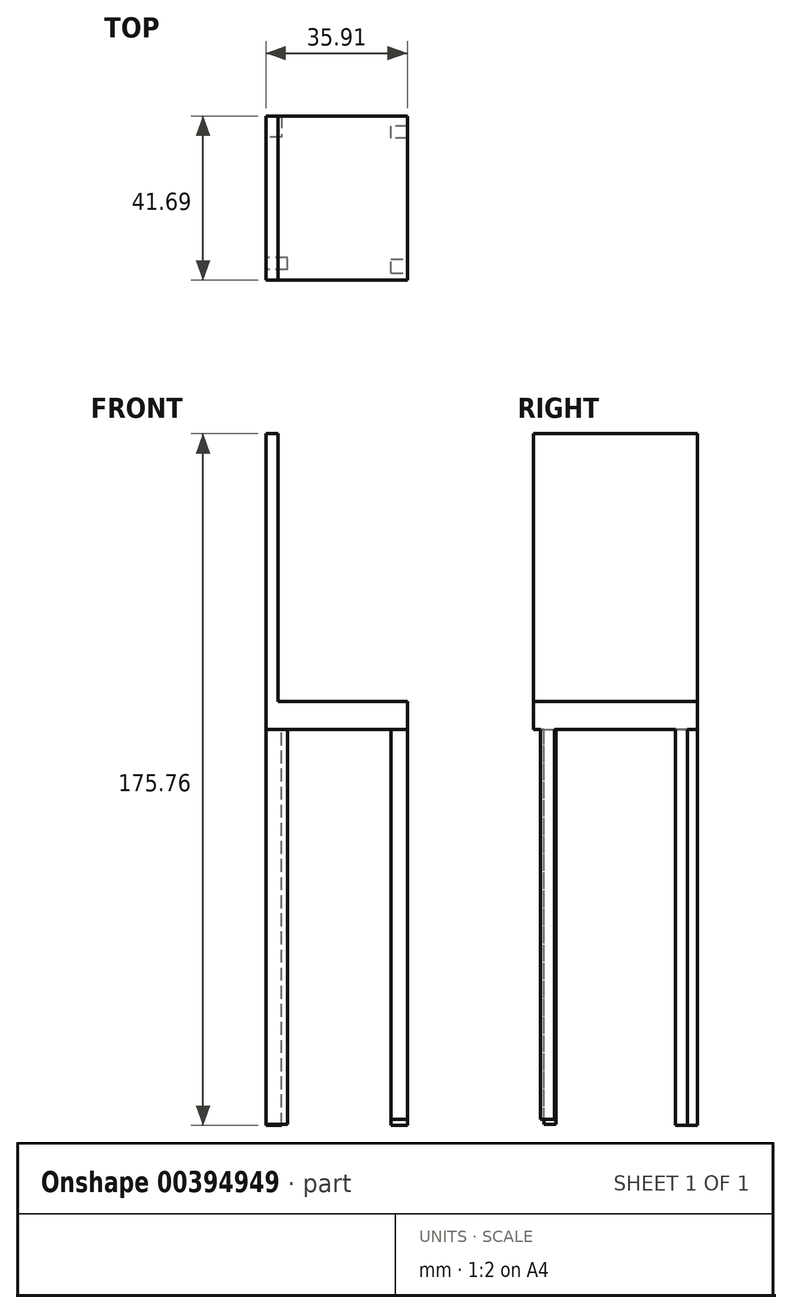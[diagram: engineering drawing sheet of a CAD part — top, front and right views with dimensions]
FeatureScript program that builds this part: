
annotation { "Feature Type Name" : "Feature", "Feature Type Description" : "" }
export const myFeature = defineFeature(function(context is Context, id is Id, definition is map)
    precondition{}
    {
        {
            var Q0;
            Q0=qCreatedBy(makeId("Top.planeOp"),FACE);
            var sketch = newSketch(context, id + "F0", { "sketchPlane" : qUnion([Q0])});
            skLineSegment(sketch, "E0.bottom", {"start": v(-61.68, 12.98) * mm, "end": v(-25.77, 12.98) * mm});
            skLineSegment(sketch, "E0.top", {"start": v(-61.68, -28.7) * mm, "end": v(-25.77, -28.7) * mm});
            skLineSegment(sketch, "E0.left", {"start": v(-61.68, 12.98) * mm, "end": v(-61.68, -28.7) * mm});
            skLineSegment(sketch, "E0.right", {"start": v(-25.77, 12.98) * mm, "end": v(-25.77, -28.7) * mm});
            skSolve(sketch);
        }
        {
            var Q0;
            Q0 = qSketchRegion(id + "F0", true);
            extrude(context, id + "F1", {"entities" : qUnion([Q0]), "depth" : 7.11 * mm});
        }
        {
            var Q0;
            Q0=makeQuery(id+"F1.opExtrude","CAP_FACE",FACE,{"disambiguationData":[OSD([sQuery(id+"F0.wireOp",EDGE,"E0.bottom"),sQuery(id+"F0.wireOp",EDGE,"E0.top"),sQuery(id+"F0.wireOp",EDGE,"E0.left"),sQuery(id+"F0.wireOp",EDGE,"E0.right")])],"isStart":true});
            var sketch = newSketch(context, id + "F2", { "sketchPlane" : qUnion([Q0])});
            skLineSegment(sketch, "E1.bottom", {"start": v(-29.9, 26.94) * mm, "end": v(-25.77, 26.94) * mm});
            skLineSegment(sketch, "E1.top", {"start": v(-29.9, 23.39) * mm, "end": v(-25.77, 23.39) * mm});
            skLineSegment(sketch, "E1.left", {"start": v(-29.9, 26.94) * mm, "end": v(-29.9, 23.39) * mm});
            skLineSegment(sketch, "E1.right", {"start": v(-25.77, 26.94) * mm, "end": v(-25.77, 23.39) * mm});
            skSolve(sketch);
        }
        {
            var Q0;
            Q0 = qSketchRegion(id + "F2", true);
            extrude(context, id + "F3", {"entities" : qUnion([Q0]), "operationType" : NewBodyOperationType.ADD, "depth" : 99.06 * mm});
        }
        {
            var Q0;
            Q0=makeQuery(id+"F1.opExtrude","CAP_FACE",FACE,{"disambiguationData":[OSD([sQuery(id+"F0.wireOp",EDGE,"E0.bottom"),sQuery(id+"F0.wireOp",EDGE,"E0.top"),sQuery(id+"F0.wireOp",EDGE,"E0.left"),sQuery(id+"F0.wireOp",EDGE,"E0.right")])],"isStart":true});
            var sketch = newSketch(context, id + "F4", { "sketchPlane" : qUnion([Q0])});
            skLineSegment(sketch, "E2.bottom", {"start": v(-25.77, -7.4) * mm, "end": v(-29.9, -7.4) * mm});
            skLineSegment(sketch, "E2.top", {"start": v(-25.77, -10.48) * mm, "end": v(-29.9, -10.48) * mm});
            skLineSegment(sketch, "E2.left", {"start": v(-25.77, -7.4) * mm, "end": v(-25.77, -10.48) * mm});
            skLineSegment(sketch, "E2.right", {"start": v(-29.9, -7.4) * mm, "end": v(-29.9, -10.48) * mm});
            skSolve(sketch);
        }
        {
            var Q0;
            Q0 = qSketchRegion(id + "F4", true);
            extrude(context, id + "F5", {"entities" : qUnion([Q0]), "operationType" : NewBodyOperationType.ADD, "depth" : 100.58 * mm});
        }
        {
            var Q0;
            Q0=makeQuery(id+"F1.opExtrude","CAP_FACE",FACE,{"disambiguationData":[OSD([sQuery(id+"F0.wireOp",EDGE,"E0.bottom"),sQuery(id+"F0.wireOp",EDGE,"E0.top"),sQuery(id+"F0.wireOp",EDGE,"E0.left"),sQuery(id+"F0.wireOp",EDGE,"E0.right")])],"isStart":true});
            var sketch = newSketch(context, id + "F6", { "sketchPlane" : qUnion([Q0])});
            skLineSegment(sketch, "E3.bottom", {"start": v(-57.7, -12.98) * mm, "end": v(-61.68, -12.98) * mm});
            skLineSegment(sketch, "E3.top", {"start": v(-57.7, -7.65) * mm, "end": v(-61.68, -7.65) * mm});
            skLineSegment(sketch, "E3.left", {"start": v(-57.7, -12.98) * mm, "end": v(-57.7, -7.65) * mm});
            skLineSegment(sketch, "E3.right", {"start": v(-61.68, -12.98) * mm, "end": v(-61.68, -7.65) * mm});
            skSolve(sketch);
        }
        {
            var Q0;
            Q0 = qSketchRegion(id + "F6", true);
            extrude(context, id + "F7", {"entities" : qUnion([Q0]), "operationType" : NewBodyOperationType.ADD, "depth" : 100.58 * mm});
        }
        {
            var Q0;
            Q0=makeQuery(id+"F1.opExtrude","CAP_FACE",FACE,{"disambiguationData":[OSD([sQuery(id+"F0.wireOp",EDGE,"E0.bottom"),sQuery(id+"F0.wireOp",EDGE,"E0.top"),sQuery(id+"F0.wireOp",EDGE,"E0.left"),sQuery(id+"F0.wireOp",EDGE,"E0.right")])],"isStart":true});
            var sketch = newSketch(context, id + "F8", { "sketchPlane" : qUnion([Q0])});
            skLineSegment(sketch, "E4.bottom", {"start": v(-56.22, 26.04) * mm, "end": v(-61.68, 26.04) * mm});
            skLineSegment(sketch, "E4.top", {"start": v(-56.22, 22.97) * mm, "end": v(-61.68, 22.97) * mm});
            skLineSegment(sketch, "E4.left", {"start": v(-56.22, 26.04) * mm, "end": v(-56.22, 22.97) * mm});
            skLineSegment(sketch, "E4.right", {"start": v(-61.68, 26.04) * mm, "end": v(-61.68, 22.97) * mm});
            skSolve(sketch);
        }
        {
            var Q0;
            Q0 = qSketchRegion(id + "F8", true);
            extrude(context, id + "F9", {"entities" : qUnion([Q0]), "operationType" : NewBodyOperationType.ADD, "depth" : 100.33 * mm});
        }
        {
            var Q0;
            Q0=makeQuery(id+"F1.opExtrude","CAP_FACE",FACE,{"disambiguationData":[OSD([sQuery(id+"F0.wireOp",EDGE,"E0.bottom"),sQuery(id+"F0.wireOp",EDGE,"E0.top"),sQuery(id+"F0.wireOp",EDGE,"E0.left"),sQuery(id+"F0.wireOp",EDGE,"E0.right")])],"isStart":false});
            var sketch = newSketch(context, id + "F10", { "sketchPlane" : qUnion([Q0])});
            skLineSegment(sketch, "E5.bottom", {"start": v(-58.62, -28.7) * mm, "end": v(-61.68, -28.7) * mm});
            skLineSegment(sketch, "E5.top", {"start": v(-58.62, 12.98) * mm, "end": v(-61.68, 12.98) * mm});
            skLineSegment(sketch, "E5.left", {"start": v(-58.62, -28.7) * mm, "end": v(-58.62, 12.98) * mm});
            skLineSegment(sketch, "E5.right", {"start": v(-61.68, -28.7) * mm, "end": v(-61.68, 12.98) * mm});
            skSolve(sketch);
        }
        {
            var Q0;
            Q0 = qSketchRegion(id + "F10", true);
            extrude(context, id + "F11", {"entities" : qUnion([Q0]), "operationType" : NewBodyOperationType.ADD, "depth" : 68.07 * mm});
        }
    });
